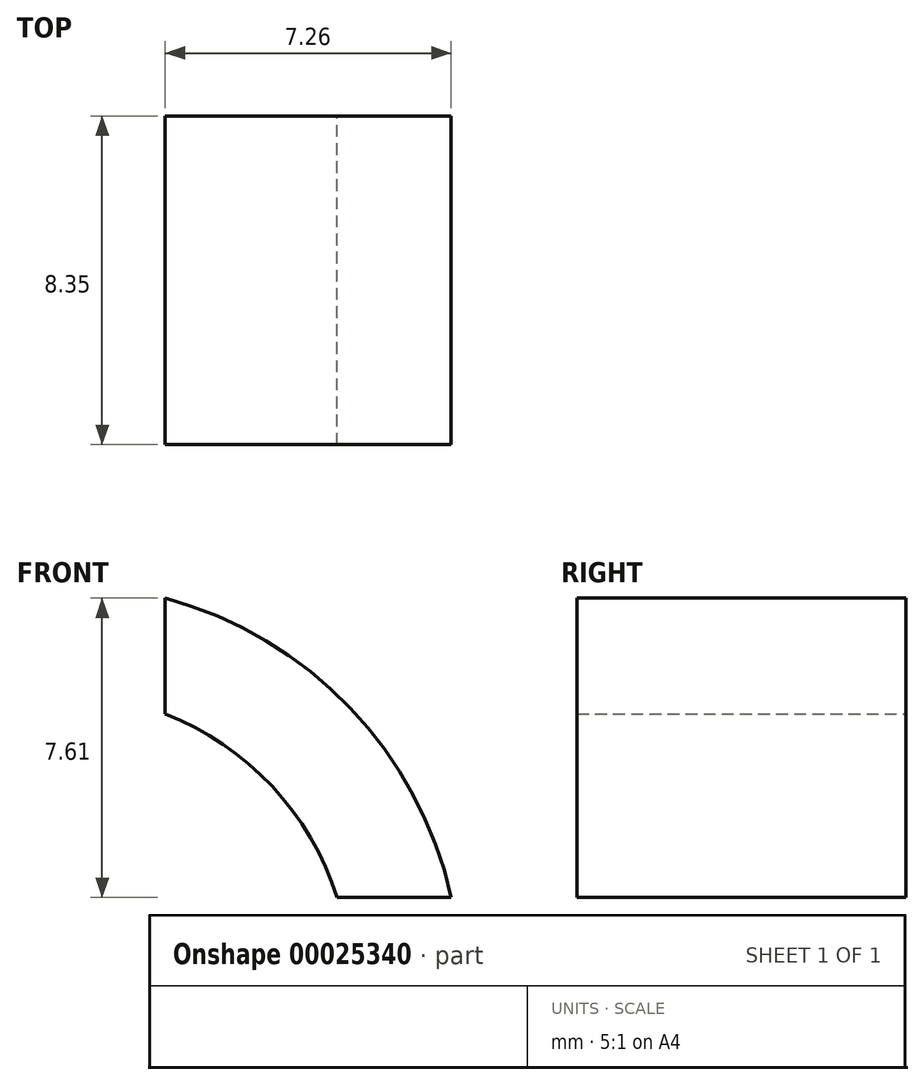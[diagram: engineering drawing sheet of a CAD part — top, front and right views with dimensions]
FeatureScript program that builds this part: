
annotation { "Feature Type Name" : "Feature", "Feature Type Description" : "" }
export const myFeature = defineFeature(function(context is Context, id is Id, definition is map)
    precondition{}
    {
        {
            var Q0;
            Q0=qCreatedBy(makeId("Front.planeOp"),FACE);
            var sketch = newSketch(context, id + "F0", { "sketchPlane" : qUnion([Q0])});
            skLineSegment(sketch, "E0", {"start": v(2.65, 6.86) * mm, "end": v(2.65, 9.8) * mm});
            skLineSegment(sketch, "E1", {"start": v(7.01, 2.2) * mm, "end": v(9.91, 2.2) * mm});
            skLineSegment(sketch, "E2", {"start": v(2.65, 9.8) * mm, "end": v(2.65, 9.8) * mm});
            skArc(sketch, "E3", {"start": v(7.01, 2.2) * mm, "mid": v(5.36, 5.03) * mm, "end": v(2.65, 6.86) * mm});
            skArc(sketch, "E4", {"start": v(9.91, 2.2) * mm, "mid": v(7.34, 7.02) * mm, "end": v(2.65, 9.8) * mm});
            skSolve(sketch);
        }
        {
            var Q0;
            Q0 = qSketchRegion(id + "F0", true);
            extrude(context, id + "F1", {"entities" : qUnion([Q0]), "depth" : 8.35 * mm});
        }
    });
